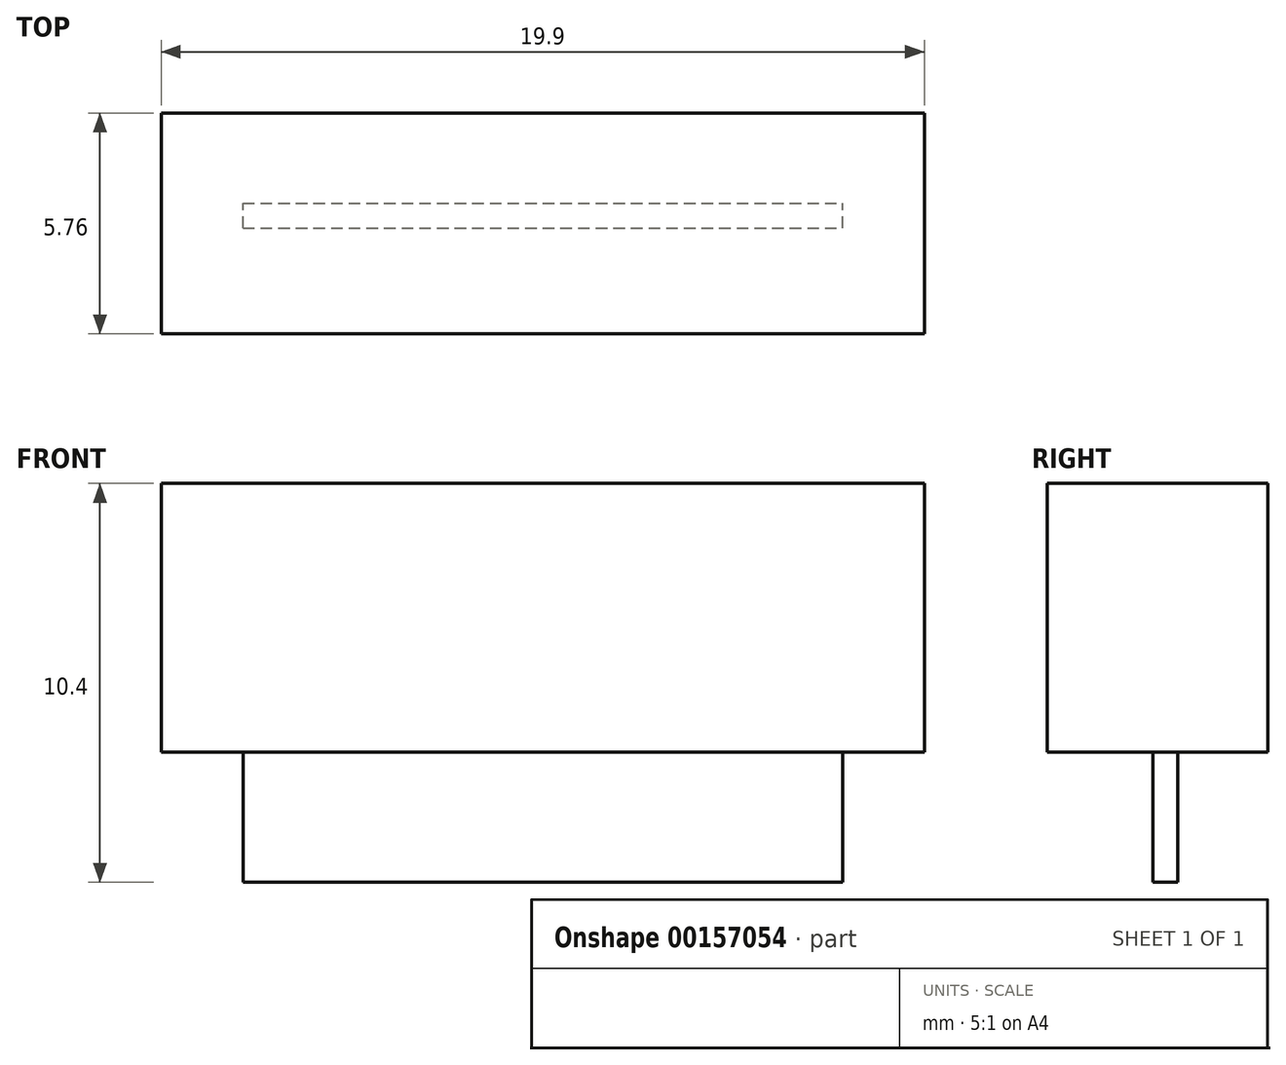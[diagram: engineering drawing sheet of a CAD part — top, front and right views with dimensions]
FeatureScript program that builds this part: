
annotation { "Feature Type Name" : "Feature", "Feature Type Description" : "" }
export const myFeature = defineFeature(function(context is Context, id is Id, definition is map)
    precondition{}
    {
        {
            var Q0;
            Q0=qCreatedBy(makeId("Top.planeOp"),FACE);
            var sketch = newSketch(context, id + "F0", { "sketchPlane" : qUnion([Q0])});
            skLineSegment(sketch, "E0.bottom", {"start": v(9.95, 2.88) * mm, "end": v(-9.95, 2.88) * mm});
            skLineSegment(sketch, "E0.top", {"start": v(9.95, -2.88) * mm, "end": v(-9.95, -2.88) * mm});
            skLineSegment(sketch, "E0.left", {"start": v(9.95, 2.88) * mm, "end": v(9.95, -2.88) * mm});
            skLineSegment(sketch, "E0.right", {"start": v(-9.95, 2.88) * mm, "end": v(-9.95, -2.88) * mm});
            skPoint(sketch, "E0.middle", {"position": v(0, 0) * mm});
            skSolve(sketch);
        }
        {
            var Q0;
            Q0=makeQuery(id+"F0.imprint","IMPRINT",FACE,{"disambiguationData":[TD([[makeQuery(id+"F0.imprint","IMPRINT",EDGE,{"derivedFrom":sQuery(id+"F0.wireOp",EDGE,"E0.bottom")}),1.0]])]});
            extrude(context, id + "F1", {"entities" : qUnion([Q0]), "depth" : 7 * mm});
        }
        {
            var Q0;
            Q0=makeQuery(id+"F1.opExtrude","CAP_FACE",FACE,{"disambiguationData":[OSD([sQuery(id+"F0.wireOp",EDGE,"E0.bottom"),sQuery(id+"F0.wireOp",EDGE,"E0.top"),sQuery(id+"F0.wireOp",EDGE,"E0.left"),sQuery(id+"F0.wireOp",EDGE,"E0.right")])],"isStart":true});
            var sketch = newSketch(context, id + "F2", { "sketchPlane" : qUnion([Q0])});
            skPoint(sketch, "E1.middle", {"position": v(0, 0) * mm});
            skLineSegment(sketch, "E2.bottom", {"start": v(-7.82, 0.11) * mm, "end": v(7.82, 0.11) * mm});
            skLineSegment(sketch, "E2.top", {"start": v(-7.82, -0.53) * mm, "end": v(7.82, -0.52) * mm});
            skLineSegment(sketch, "E2.left", {"start": v(-7.82, 0.11) * mm, "end": v(-7.82, -0.53) * mm});
            skLineSegment(sketch, "E2.right", {"start": v(7.82, 0.11) * mm, "end": v(7.82, -0.53) * mm});
            skLineSegment(sketch, "E3", {"start": v(-7.82, -0.53) * mm, "end": v(-9.95, -0.53) * mm, "construction": true});
            skLineSegment(sketch, "E4", {"start": v(7.82, -0.52) * mm, "end": v(9.95, -0.53) * mm, "construction": true});
            skSolve(sketch);
        }
        {
            var Q0;
            Q0 = qSketchRegion(id + "F2", true);
            extrude(context, id + "F3", {"entities" : qUnion([Q0]), "operationType" : NewBodyOperationType.ADD, "depth" : 3.4 * mm});
        }
    });
